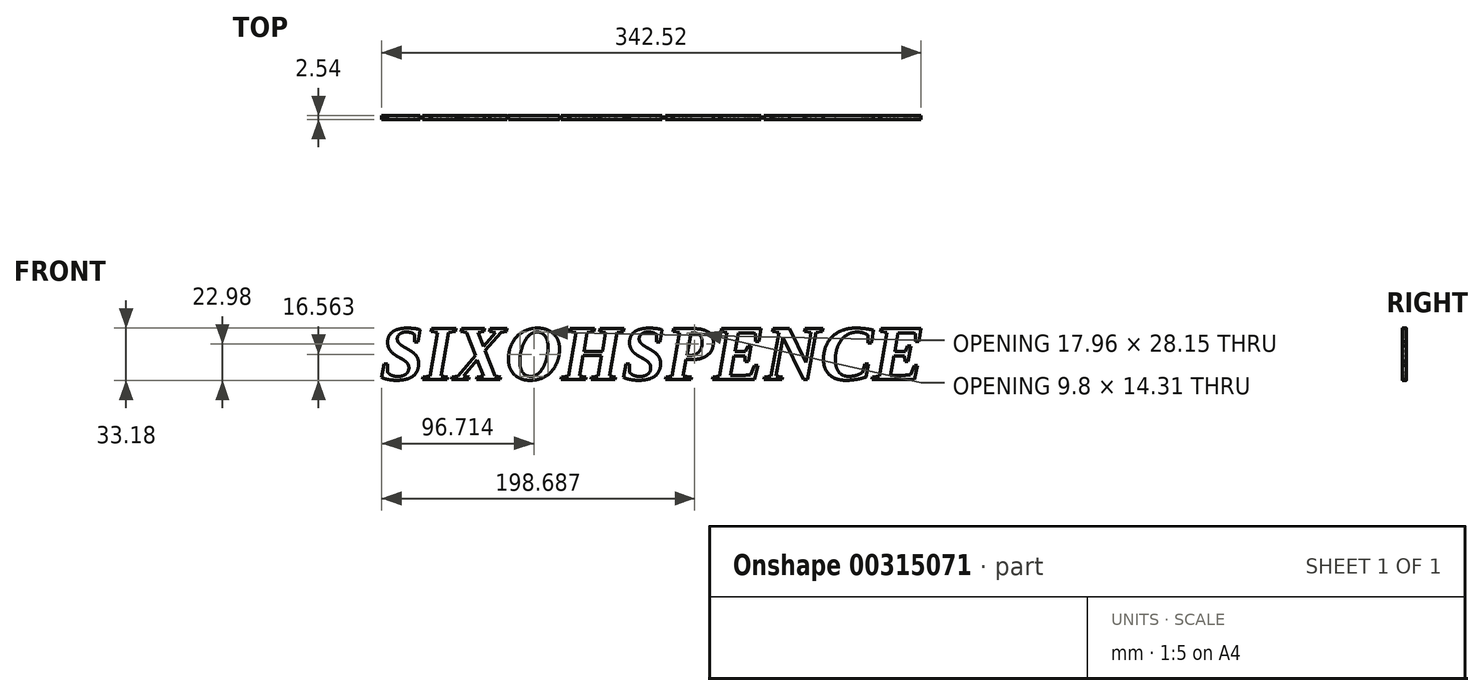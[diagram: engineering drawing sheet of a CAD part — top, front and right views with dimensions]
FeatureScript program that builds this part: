
annotation { "Feature Type Name" : "Feature", "Feature Type Description" : "" }
export const myFeature = defineFeature(function(context is Context, id is Id, definition is map)
    precondition{}
    {
        {
            var Q0;
            Q0=qCreatedBy(makeId("Front.planeOp"),FACE);
            var sketch = newSketch(context, id + "F0", { "sketchPlane" : qUnion([Q0])});
            skText(sketch, "E0", { "text": "SIXOHSPENCE", "fontName": "Tinos-BoldItalic.ttf"});
            const initialGuessF0  = {"E0": [-0.06476, 0, 1, 0, 0.03554]};
            skSetInitialGuess(sketch, initialGuessF0);
            skSolve(sketch);
        }
        {
            var Q0;
            Q0 = qSketchRegion(id + "F0", true);
            extrude(context, id + "F1", {"entities" : qUnion([Q0]), "depth" : 2.54 * mm});
        }
    });
